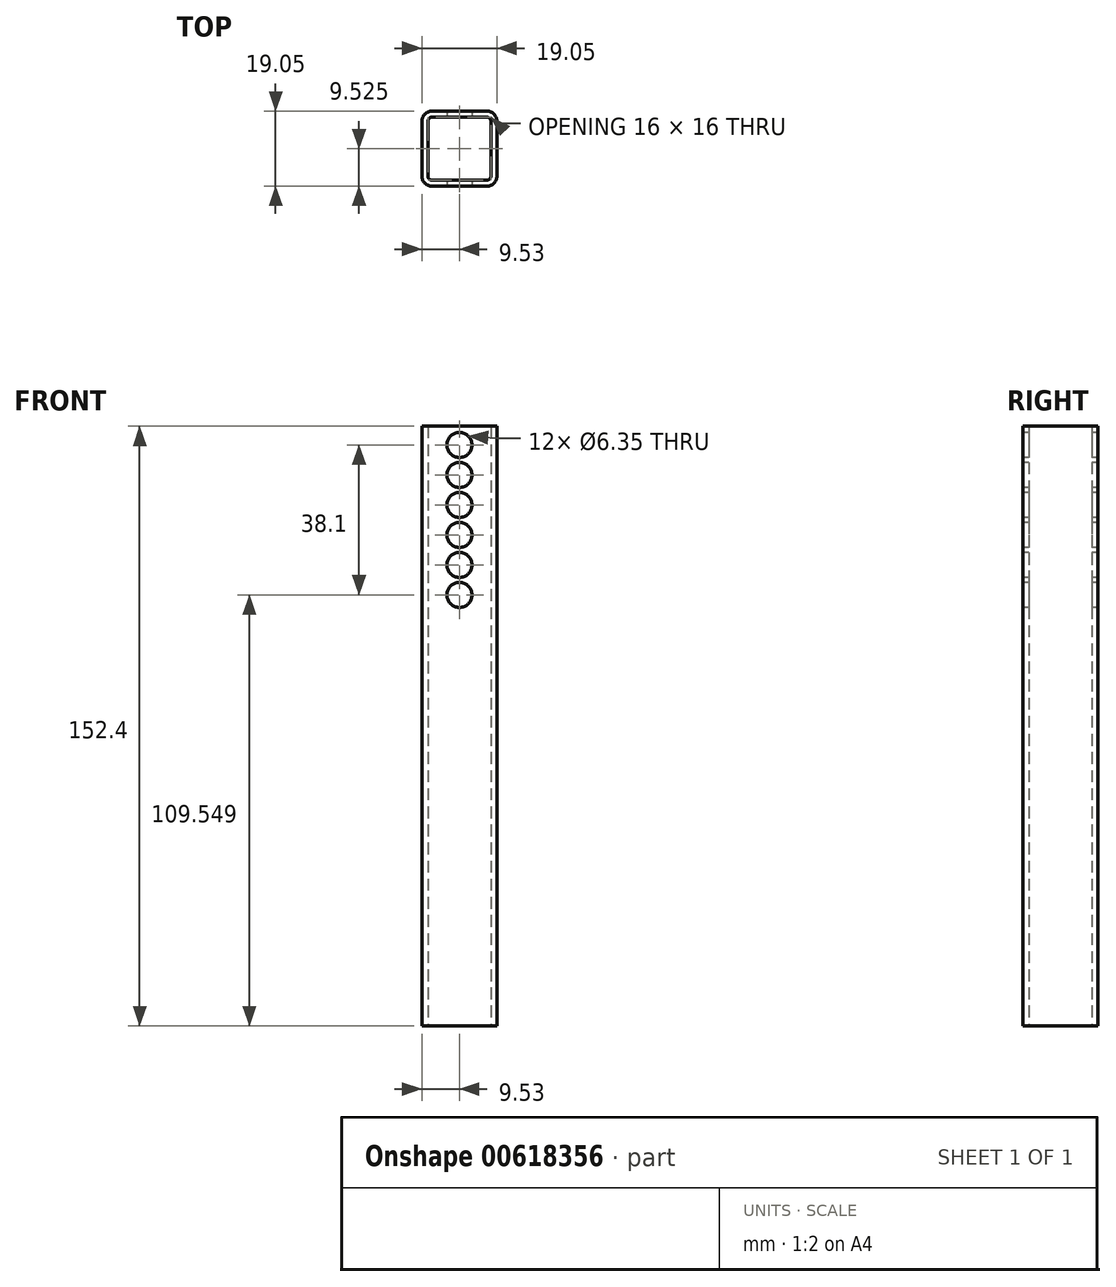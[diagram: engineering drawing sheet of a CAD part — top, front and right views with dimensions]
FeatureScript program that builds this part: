
annotation { "Feature Type Name" : "Feature", "Feature Type Description" : "" }
export const myFeature = defineFeature(function(context is Context, id is Id, definition is map)
    precondition{}
    {
        {
            var Q0;
            Q0=qCreatedBy(makeId("Top.planeOp"),FACE);
            var sketch = newSketch(context, id + "F0", { "sketchPlane" : qUnion([Q0])});
            skLineSegment(sketch, "E0.bottom", {"start": v(3.75, 0) * mm, "end": v(17.72, 0) * mm});
            skLineSegment(sketch, "E0.top", {"start": v(3.75, 19.05) * mm, "end": v(17.72, 19.05) * mm});
            skLineSegment(sketch, "E0.left", {"start": v(1.21, 2.54) * mm, "end": v(1.21, 16.51) * mm});
            skLineSegment(sketch, "E0.right", {"start": v(20.26, 2.54) * mm, "end": v(20.26, 16.51) * mm});
            skPoint(sketch, "E1.visualSharp", {"position": v(1.21, 19.05) * mm});
            skArc(sketch, "E1.filletArc", {"start": v(3.75, 19.05) * mm, "mid": v(1.96, 18.3) * mm, "end": v(1.21, 16.51) * mm});
            skPoint(sketch, "E2.visualSharp", {"position": v(20.26, 19.05) * mm});
            skArc(sketch, "E2.filletArc", {"start": v(20.26, 16.51) * mm, "mid": v(19.52, 18.3) * mm, "end": v(17.72, 19.05) * mm});
            skPoint(sketch, "E3.visualSharp", {"position": v(20.26, 0) * mm});
            skArc(sketch, "E3.filletArc", {"start": v(17.72, 0) * mm, "mid": v(19.52, 0.74) * mm, "end": v(20.26, 2.54) * mm});
            skPoint(sketch, "E4.visualSharp", {"position": v(1.21, 0) * mm});
            skArc(sketch, "E4.filletArc", {"start": v(1.21, 2.54) * mm, "mid": v(1.96, 0.74) * mm, "end": v(3.75, 0) * mm});
            skArc(sketch, "E5.0", {"start": v(2.74, 2.54) * mm, "mid": v(3.04, 1.82) * mm, "end": v(3.75, 1.52) * mm});
            skLineSegment(sketch, "E5.1", {"start": v(2.74, 2.54) * mm, "end": v(2.74, 16.51) * mm});
            skLineSegment(sketch, "E5.2", {"start": v(3.75, 1.52) * mm, "end": v(17.72, 1.52) * mm});
            skArc(sketch, "E5.3", {"start": v(3.75, 17.53) * mm, "mid": v(3.04, 17.23) * mm, "end": v(2.74, 16.51) * mm});
            skArc(sketch, "E5.4", {"start": v(17.72, 1.52) * mm, "mid": v(18.44, 1.82) * mm, "end": v(18.74, 2.54) * mm});
            skLineSegment(sketch, "E5.5", {"start": v(18.74, 2.54) * mm, "end": v(18.74, 16.51) * mm});
            skArc(sketch, "E5.6", {"start": v(18.74, 16.51) * mm, "mid": v(18.44, 17.23) * mm, "end": v(17.72, 17.53) * mm});
            skLineSegment(sketch, "E5.7", {"start": v(3.75, 17.53) * mm, "end": v(17.72, 17.53) * mm});
            skSolve(sketch);
        }
        {
            var Q0;
            Q0 = qSketchRegion(id + "F0", true);
            extrude(context, id + "F1", {"entities" : qUnion([Q0]), "depth" : 152.4 * mm, "offsetDistance" : 25.4 * mm});
        }
        {
            var Q0;
            Q0=makeQuery(id+"F1.opExtrude","SWEPT_FACE",FACE,{"disambiguationData":[OSD([sQuery(id+"F0.wireOp",EDGE,"E0.bottom")])]});
            var sketch = newSketch(context, id + "F2", { "sketchPlane" : qUnion([Q0])});
            skCircle(sketch, "E6", {"center": v(10.74, 147.65) * mm, "radius": 3.18 * mm});
            skPoint(sketch, "E6.centerSnap0", {"position": v(10.74, 152.4) * mm});
            skCircle(sketch, "E7.1.0.0", {"center": v(10.74, 140.03) * mm, "radius": 3.18 * mm});
            skCircle(sketch, "E7.2.0.0", {"center": v(10.74, 132.4) * mm, "radius": 3.18 * mm});
            skLineSegment(sketch, "E7.direction1", {"start": v(10.74, 147.65) * mm, "end": v(10.74, 140.03) * mm, "construction": true});
            skCircle(sketch, "E8.0.3.0", {"center": v(10.74, 124.79) * mm, "radius": 3.18 * mm});
            skCircle(sketch, "E8.0.4.0", {"center": v(10.74, 117.17) * mm, "radius": 3.18 * mm});
            skCircle(sketch, "E8.0.5.0", {"center": v(10.74, 109.55) * mm, "radius": 3.18 * mm});
            skSolve(sketch);
        }
        {
            var Q0;
            Q0 = qSketchRegion(id + "F2", true);
            extrude(context, id + "F3", {"entities" : qUnion([Q0]), "operationType" : NewBodyOperationType.REMOVE, "oppositeDirection" : true, "depth" : 25.4 * mm, "offsetDistance" : 25.4 * mm});
        }
    });
